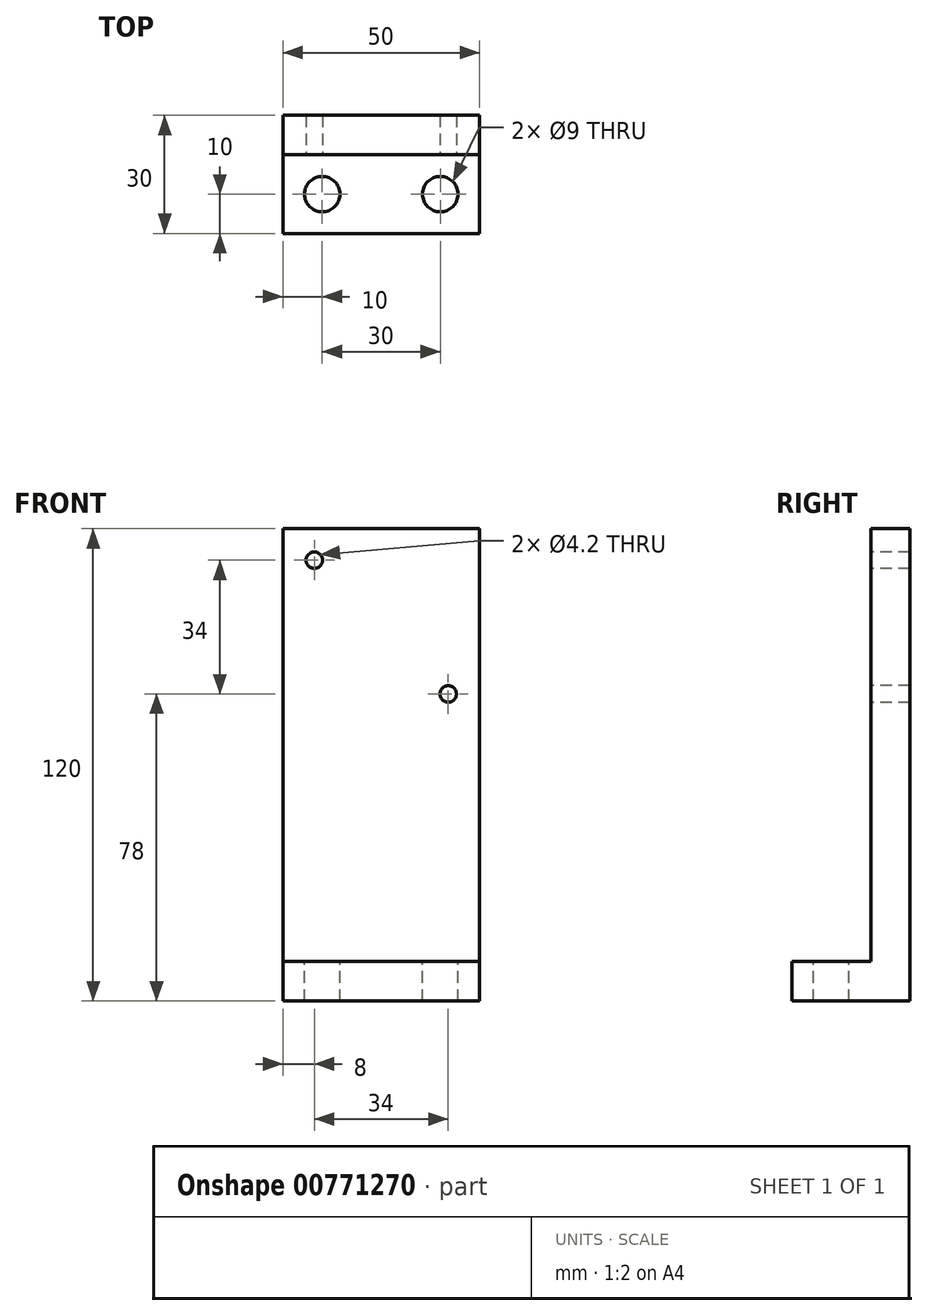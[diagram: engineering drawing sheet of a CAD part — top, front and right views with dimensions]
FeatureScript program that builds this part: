
annotation { "Feature Type Name" : "Feature", "Feature Type Description" : "" }
export const myFeature = defineFeature(function(context is Context, id is Id, definition is map)
    precondition{}
    {
        {
            var Q0;
            Q0=qCreatedBy(makeId("Front.planeOp"),FACE);
            var sketch = newSketch(context, id + "F0", { "sketchPlane" : qUnion([Q0])});
            skLineSegment(sketch, "E0", {"start": v(0, 0) * mm, "end": v(50, 0) * mm});
            skLineSegment(sketch, "E1", {"start": v(50, 0) * mm, "end": v(50, -120) * mm});
            skLineSegment(sketch, "E2", {"start": v(50, -120) * mm, "end": v(0, -120) * mm});
            skLineSegment(sketch, "E3", {"start": v(0, -120) * mm, "end": v(0, 0) * mm});
            skSolve(sketch);
        }
        {
            var Q0;
            Q0=makeQuery(id+"F0.imprint","IMPRINT",FACE,{"disambiguationData":[TD([[makeQuery(id+"F0.imprint","IMPRINT",EDGE,{"derivedFrom":sQuery(id+"F0.wireOp",EDGE,"E0")}),-1.0]])]});
            extrude(context, id + "F1", {"entities" : qUnion([Q0]), "depth" : 10 * mm, "offsetDistance" : 25.4 * mm});
        }
        {
            var Q0;
            Q0=makeQuery(id+"F1.opExtrude","CAP_FACE",FACE,{"disambiguationData":[OSD([sQuery(id+"F0.wireOp",EDGE,"E0"),sQuery(id+"F0.wireOp",EDGE,"E1"),sQuery(id+"F0.wireOp",EDGE,"E2"),sQuery(id+"F0.wireOp",EDGE,"E3")])],"isStart":false});
            var sketch = newSketch(context, id + "F2", { "sketchPlane" : qUnion([Q0])});
            skLineSegment(sketch, "E4", {"start": v(50, -120) * mm, "end": v(50, -110) * mm});
            skLineSegment(sketch, "E5", {"start": v(50, -110) * mm, "end": v(0, -110) * mm});
            skLineSegment(sketch, "E6", {"start": v(0, -110) * mm, "end": v(0, -120) * mm});
            skLineSegment(sketch, "E7", {"start": v(0, -120) * mm, "end": v(50, -120) * mm});
            skSolve(sketch);
        }
        {
            var Q0;
            Q0=makeQuery(id+"F2.imprint","IMPRINT",FACE,{"disambiguationData":[TD([[makeQuery(id+"F2.imprint","IMPRINT",EDGE,{"derivedFrom":sQuery(id+"F2.wireOp",EDGE,"E4")}),-1.0]])]});
            extrude(context, id + "F3", {"entities" : qUnion([Q0]), "operationType" : NewBodyOperationType.ADD, "depth" : 20 * mm, "offsetDistance" : 25.4 * mm});
        }
        {
            var Q0;
            Q0=makeQuery(id+"F3.opExtrude","SWEPT_FACE",FACE,{"disambiguationData":[OSD([sQuery(id+"F2.wireOp",EDGE,"E5")])]});
            var sketch = newSketch(context, id + "F4", { "sketchPlane" : qUnion([Q0])});
            skPoint(sketch, "E8", {"position": v(10, -20) * mm});
            skPoint(sketch, "E9", {"position": v(40, -20) * mm});
            skCircle(sketch, "E10", {"center": v(10, -20) * mm, "radius": 4.5 * mm});
            skCircle(sketch, "E11", {"center": v(40, -20) * mm, "radius": 4.5 * mm});
            skSolve(sketch);
        }
        {
            var Q0;
            Q0 = qSketchRegion(id + "F4", true);
            extrude(context, id + "F5", {"entities" : qUnion([Q0]), "operationType" : NewBodyOperationType.REMOVE, "endBound" : BoundingType.THROUGH_ALL, "oppositeDirection" : true, "depth" : 25.4 * mm, "offsetDistance" : 25.4 * mm});
        }
        {
            var Q0;
            Q0=makeQuery(id+"F1.opExtrude","CAP_FACE",FACE,{"disambiguationData":[OSD([sQuery(id+"F0.wireOp",EDGE,"E0"),sQuery(id+"F0.wireOp",EDGE,"E1"),sQuery(id+"F0.wireOp",EDGE,"E2"),sQuery(id+"F0.wireOp",EDGE,"E3")])],"isStart":false});
            var sketch = newSketch(context, id + "F6", { "sketchPlane" : qUnion([Q0])});
            skPoint(sketch, "E12", {"position": v(8, -8) * mm});
            skPoint(sketch, "E13", {"position": v(42, -42) * mm});
            skSolve(sketch);
        }
        {
            var Q0;
            Q0=sQuery(id+"F6.wireOp",VERTEX,"E12");
            var Q1;
            Q1=sQuery(id+"F6.wireOp",VERTEX,"E13");
            var Q2;
            Q2=makeQuery(id+"F1.opExtrude","SWEPT_BODY",BODY,{"disambiguationData":[OSD([sQuery(id+"F0.wireOp",EDGE,"E0"),sQuery(id+"F0.wireOp",EDGE,"E1"),sQuery(id+"F0.wireOp",EDGE,"E2"),sQuery(id+"F0.wireOp",EDGE,"E3")])]});
            hole(context, id + "F7", {"style" : HoleStyle.SIMPLE, "endStyle" : HoleEndStyle.THROUGH, "standardTappedOrClearance" : lookupTablePath({ "standard" : "ISO", "engagement" : "75%", "pitch" : "0.8 mm", "size" : "M5", "type" : "Tapped" }), "standardBlindInLast" : lookupTablePath({ "standard" : "ISO", "engagement" : "75%", "pitch" : "0.8 mm", "size" : "M5", "type" : "Tapped" }), "holeDiameter" : 4.2 * mm, "majorDiameter" : 5 * mm, "showTappedDepth" : true, "isTappedThrough" : true, "tappedDepth" : 12.7 * mm, "tapClearance" : 3, "locations" : qUnion([Q0, Q1]), "scope" : qUnion([Q2])});
        }
    });
